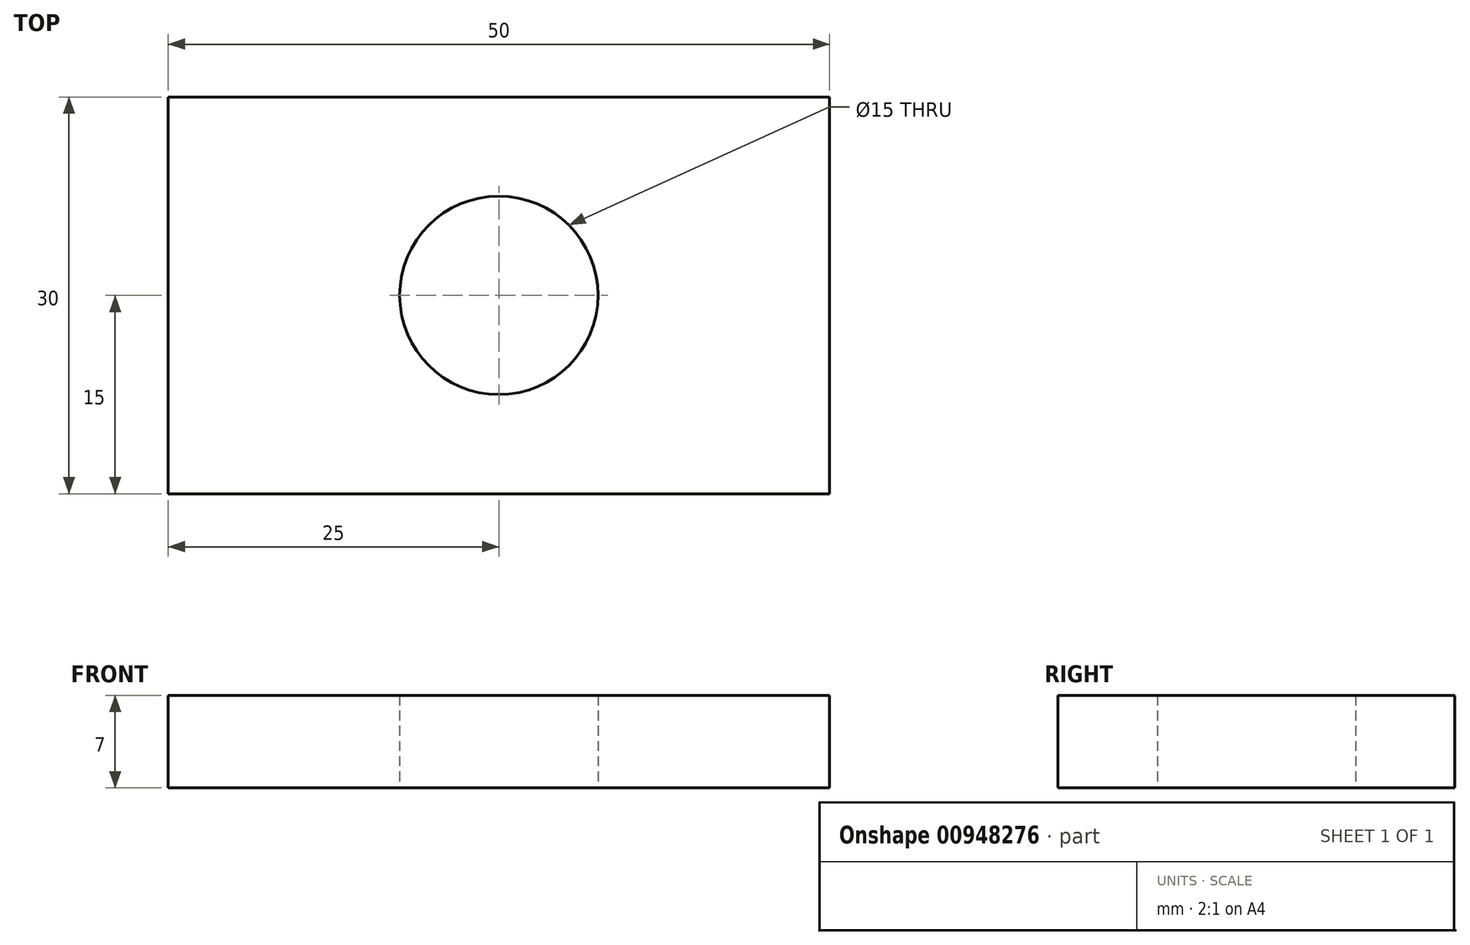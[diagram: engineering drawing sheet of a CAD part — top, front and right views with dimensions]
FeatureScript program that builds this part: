
annotation { "Feature Type Name" : "Feature", "Feature Type Description" : "" }
export const myFeature = defineFeature(function(context is Context, id is Id, definition is map)
    precondition{}
    {
        {
            var Q0;
            Q0=qCreatedBy(makeId("Top.planeOp"),FACE);
            var sketch = newSketch(context, id + "F0", { "sketchPlane" : qUnion([Q0])});
            skLineSegment(sketch, "E0.bottom", {"start": v(25, -15) * mm, "end": v(-25, -15) * mm});
            skLineSegment(sketch, "E0.top", {"start": v(25, 15) * mm, "end": v(-25, 15) * mm});
            skLineSegment(sketch, "E0.left", {"start": v(25, -15) * mm, "end": v(25, 15) * mm});
            skLineSegment(sketch, "E0.right", {"start": v(-25, -15) * mm, "end": v(-25, 15) * mm});
            skPoint(sketch, "E0.middle", {"position": v(0, 0) * mm});
            skCircle(sketch, "E1", {"center": v(0, 0) * mm, "radius": 7.5 * mm});
            skSolve(sketch);
        }
        {
            var Q0;
            Q0=makeQuery(id+"F0.imprint","IMPRINT",FACE,{"disambiguationData":[TD([[makeQuery(id+"F0.imprint","IMPRINT",EDGE,{"derivedFrom":sQuery(id+"F0.wireOp",EDGE,"E0.bottom")}),-1.0]])]});
            extrude(context, id + "F1", {"entities" : qUnion([Q0]), "depth" : 7 * mm, "offsetDistance" : 25 * mm});
        }
    });
